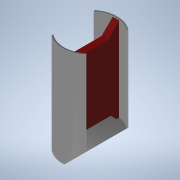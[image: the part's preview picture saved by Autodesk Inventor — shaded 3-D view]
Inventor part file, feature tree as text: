
AUTODESK INVENTOR PART (.ipt)
format: ipt  version: 2021.3 (Build 253353010, 353A)  size: 142,848 bytes
history: native  units: mm
features: extrude x5, sketch x5, plane x2, chamfer x1
ambient origin geometry x8: Origin, YZ Plane, XZ Plane, XY Plane, X Axis, Y Axis, Z Axis, Center Point
bodies: Solid1 (feature_tree), Solid2 (feature_tree)
feature tree (13):
  extrude  "Extrusion1"  Depth=121.0mm TaperAngle=0.0deg
  extrude  "Extrusion2"  Depth=103.0mm TaperAngle=0.0deg
  extrude  "Extrusion4"  Depth=15.0mm
  plane  "Work Plane1"
  plane  "Work Plane2"
  extrude  "Extrusion5"  Depth=8.0mm TaperAngle=0.0deg
  extrude  "Extrusion6"  Depth=18.0mm TaperAngle=0.0deg
  chamfer  "Chamfer5"  Distance=100.0mm
  sketch  "Sketch1"  dims[d0=66.0mm d1=121.0mm d2=0.0mm]
  sketch  "Sketch2"  dims[d3=63.0mm d4=103.0mm d5=0.0mm]
  sketch  "Sketch3"  dims[d13=25.0mm d17=15.0mm]
  sketch  "Sketch4"  dims[d19=15.0mm d20=8.0mm d21=0.0mm]
  sketch  "Sketch5"  dims[d22=20.0mm d23=-20.0mm d24=100.0mm d25=0.0mm d26=100.0mm d27=0.0mm d33=3.5mm d46=18.0mm d47=2.0mm d48=45.0deg]
